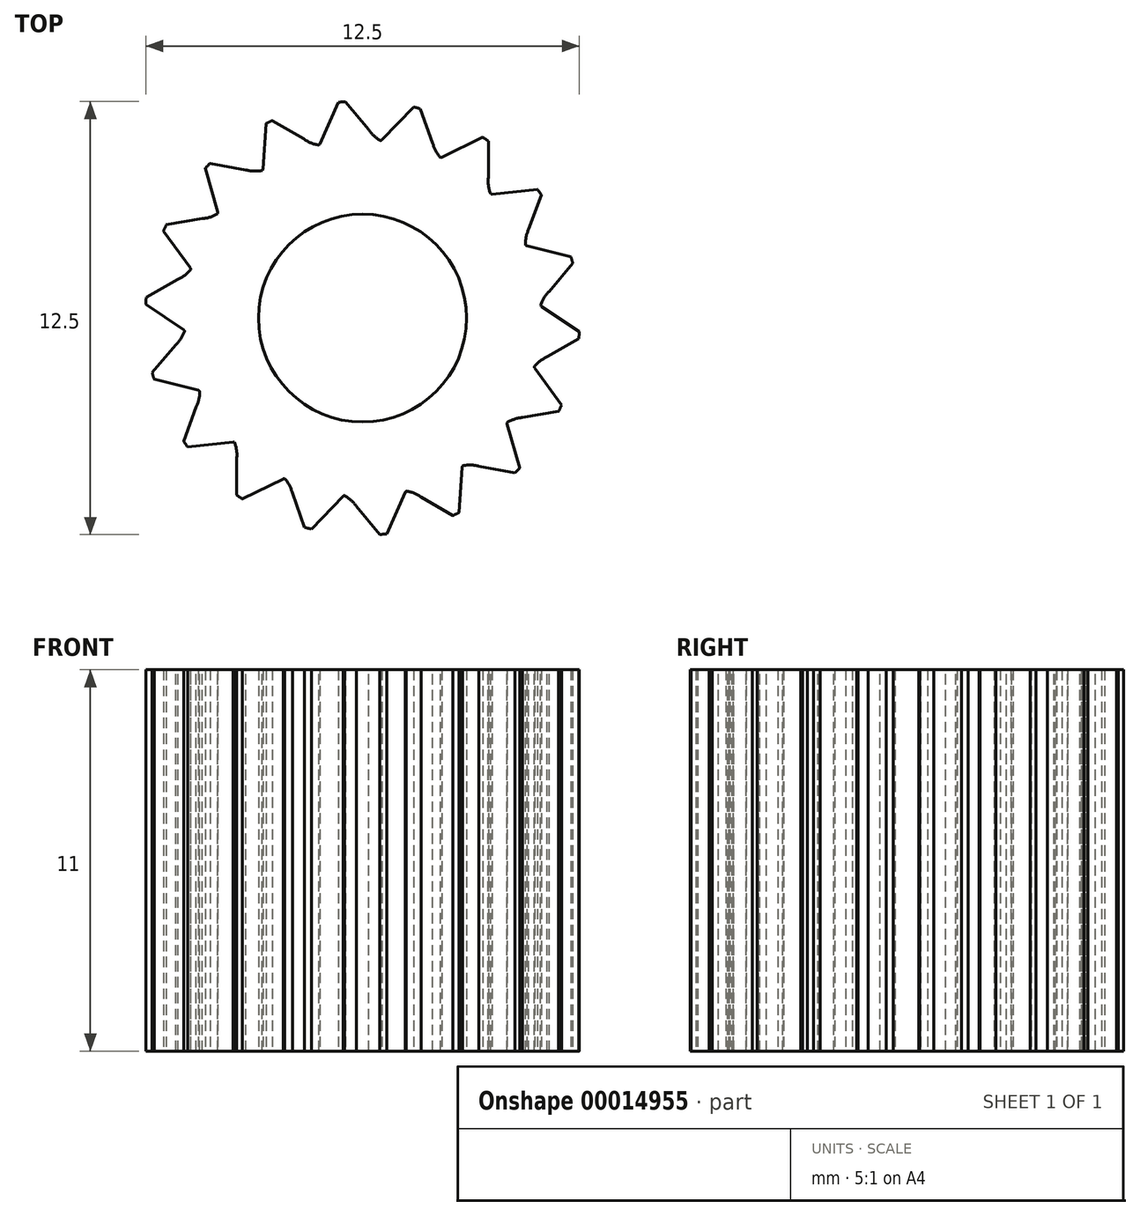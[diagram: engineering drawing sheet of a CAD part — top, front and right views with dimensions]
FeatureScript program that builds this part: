
annotation { "Feature Type Name" : "Feature", "Feature Type Description" : "" }
export const myFeature = defineFeature(function(context is Context, id is Id, definition is map)
    precondition{}
    {
        {
            var Q0;
            Q0=qCreatedBy(makeId("Top.planeOp"),FACE);
            var sketch = newSketch(context, id + "F0", { "sketchPlane" : qUnion([Q0])});
            skCircle(sketch, "E0", {"center": v(0, 0) * mm, "radius": 3 * mm});
            skCircle(sketch, "E1", {"center": v(0, 0) * mm, "radius": 6.26 * mm});
            skSolve(sketch);
        }
        {
            var Q0;
            Q0=qSketchRegion(id+"F0",true);
            extrude(context, id + "F1", {"entities" : qUnion([Q0]), "depth" : 11 * mm});
        }
        {
            var Q0;
            Q0=qCreatedBy(makeId("Front.planeOp"),FACE);
            cPlane(context, id + "F2", {"entities" : qUnion([Q0]), "cplaneType" : CPlaneType.OFFSET, "offset" : 5 * mm, "width" : 150 * mm, "height" : 150 * mm});
        }
        {
            var Q0;
            Q0=qCreatedBy(id+"F2.planeOp",FACE);
            var sketch = newSketch(context, id + "F3", { "sketchPlane" : qUnion([Q0])});
            skLineSegment(sketch, "E2.bottom", {"start": v(0, 11.05) * mm, "end": v(-1.05, 11.05) * mm});
            skLineSegment(sketch, "E2.top", {"start": v(0, 0) * mm, "end": v(-1.05, 0) * mm});
            skLineSegment(sketch, "E2.left", {"start": v(0, 11.05) * mm, "end": v(0, 0) * mm});
            skLineSegment(sketch, "E2.right", {"start": v(-1.05, 11.05) * mm, "end": v(-1.05, 0) * mm});
            skSolve(sketch);
        }
        {
            var Q0;
            Q0=makeQuery(id+"F3.imprint","IMPRINT",FACE,{"disambiguationData":[TD([[makeQuery(id+"F3.imprint","IMPRINT",EDGE,{"derivedFrom":sQuery(id+"F3.wireOp",EDGE,"E2.bottom")}),1.0]])]});
            extrude(context, id + "F4", {"entities" : qUnion([Q0]), "depth" : 2 * mm});
        }
        {
            var Q0;
            Q0=makeQuery(id+"F4.opExtrude","CAP_EDGE",EDGE,{"disambiguationData":[OSD([sQuery(id+"F3.wireOp",EDGE,"E2.left")])],"isStart":true});
            var Q1;
            Q1=makeQuery(id+"F4.opExtrude","CAP_EDGE",EDGE,{"disambiguationData":[OSD([sQuery(id+"F3.wireOp",EDGE,"E2.right")])],"isStart":true});
            fillet(context, id + "F5", {"entities" : qUnion([Q0, Q1]), "radius" : 1 * mm, "tangentPropagation" : true, "allowEdgeOverflow" : false});
        }
        {
            var Q0;
            Q0=makeQuery(id+"F4.opExtrude","SWEPT_BODY",BODY,{"disambiguationData":[OSD([sQuery(id+"F3.wireOp",EDGE,"E2.bottom"),sQuery(id+"F3.wireOp",EDGE,"E2.top"),sQuery(id+"F3.wireOp",EDGE,"E2.left"),sQuery(id+"F3.wireOp",EDGE,"E2.right")])]});
            var Q1;
            Q1=makeQuery(id+"F1.opExtrude","SWEPT_FACE",FACE,{"disambiguationData":[OSD([sQuery(id+"F0.wireOp",EDGE,"E1")])]});
            circularPattern(context, id + "F6", {"operationType" : NewBodyOperationType.REMOVE, "entities" : qUnion([Q0]), "axis" : qUnion([Q1]), "angle" : 20 * degree, "instanceCount" : round(20)});
        }
        {
            var Q0;
            Q0=makeQuery(id+"F6.boolean.opBoolean","INTERSECT",EDGE,{"derivedFrom":[makeQuery(id+"F1.opExtrude","SWEPT_FACE",FACE,{"disambiguationData":[OSD([sQuery(id+"F0.wireOp",EDGE,"E1")])]}),makeQuery(id+"F6.opPattern","COPY",FACE,{"derivedFrom":makeQuery(id+"F4.opExtrude","SWEPT_FACE",FACE,{"disambiguationData":[OSD([sQuery(id+"F3.wireOp",EDGE,"E2.left")])]}),"instanceName":"1"})]});
            var Q1;
            Q1=makeQuery(id+"F6.boolean.opBoolean","INTERSECT",EDGE,{"derivedFrom":[makeQuery(id+"F1.opExtrude","SWEPT_FACE",FACE,{"disambiguationData":[OSD([sQuery(id+"F0.wireOp",EDGE,"E1")])]}),makeQuery(id+"F4.opExtrude","SWEPT_FACE",FACE,{"disambiguationData":[OSD([sQuery(id+"F3.wireOp",EDGE,"E2.left")])]})]});
            var Q2;
            Q2=makeQuery(id+"F6.boolean.opBoolean","INTERSECT",EDGE,{"derivedFrom":[makeQuery(id+"F1.opExtrude","SWEPT_FACE",FACE,{"disambiguationData":[OSD([sQuery(id+"F0.wireOp",EDGE,"E1")])]}),makeQuery(id+"F6.opPattern","COPY",FACE,{"derivedFrom":makeQuery(id+"F4.opExtrude","SWEPT_FACE",FACE,{"disambiguationData":[OSD([sQuery(id+"F3.wireOp",EDGE,"E2.left")])]}),"instanceName":"17"})]});
            var Q3;
            Q3=makeQuery(id+"F6.boolean.opBoolean","INTERSECT",EDGE,{"derivedFrom":[makeQuery(id+"F1.opExtrude","SWEPT_FACE",FACE,{"disambiguationData":[OSD([sQuery(id+"F0.wireOp",EDGE,"E1")])]}),makeQuery(id+"F6.opPattern","COPY",FACE,{"derivedFrom":makeQuery(id+"F4.opExtrude","SWEPT_FACE",FACE,{"disambiguationData":[OSD([sQuery(id+"F3.wireOp",EDGE,"E2.left")])]}),"instanceName":"16"})]});
            var Q4;
            Q4=makeQuery(id+"F6.boolean.opBoolean","INTERSECT",EDGE,{"derivedFrom":[makeQuery(id+"F1.opExtrude","SWEPT_FACE",FACE,{"disambiguationData":[OSD([sQuery(id+"F0.wireOp",EDGE,"E1")])]}),makeQuery(id+"F6.opPattern","COPY",FACE,{"derivedFrom":makeQuery(id+"F4.opExtrude","SWEPT_FACE",FACE,{"disambiguationData":[OSD([sQuery(id+"F3.wireOp",EDGE,"E2.left")])]}),"instanceName":"2"})]});
            var Q5;
            Q5=makeQuery(id+"F6.boolean.opBoolean","INTERSECT",EDGE,{"derivedFrom":[makeQuery(id+"F1.opExtrude","SWEPT_FACE",FACE,{"disambiguationData":[OSD([sQuery(id+"F0.wireOp",EDGE,"E1")])]}),makeQuery(id+"F6.opPattern","COPY",FACE,{"derivedFrom":makeQuery(id+"F4.opExtrude","SWEPT_FACE",FACE,{"disambiguationData":[OSD([sQuery(id+"F3.wireOp",EDGE,"E2.left")])]}),"instanceName":"15"})]});
            var Q6;
            Q6=makeQuery(id+"F6.boolean.opBoolean","INTERSECT",EDGE,{"derivedFrom":[makeQuery(id+"F1.opExtrude","SWEPT_FACE",FACE,{"disambiguationData":[OSD([sQuery(id+"F0.wireOp",EDGE,"E1")])]}),makeQuery(id+"F6.opPattern","COPY",FACE,{"derivedFrom":makeQuery(id+"F4.opExtrude","SWEPT_FACE",FACE,{"disambiguationData":[OSD([sQuery(id+"F3.wireOp",EDGE,"E2.left")])]}),"instanceName":"14"})]});
            var Q7;
            Q7=makeQuery(id+"F6.boolean.opBoolean","INTERSECT",EDGE,{"derivedFrom":[makeQuery(id+"F1.opExtrude","SWEPT_FACE",FACE,{"disambiguationData":[OSD([sQuery(id+"F0.wireOp",EDGE,"E1")])]}),makeQuery(id+"F6.opPattern","COPY",FACE,{"derivedFrom":makeQuery(id+"F4.opExtrude","SWEPT_FACE",FACE,{"disambiguationData":[OSD([sQuery(id+"F3.wireOp",EDGE,"E2.left")])]}),"instanceName":"3"})]});
            var Q8;
            Q8=makeQuery(id+"F6.boolean.opBoolean","INTERSECT",EDGE,{"derivedFrom":[makeQuery(id+"F1.opExtrude","SWEPT_FACE",FACE,{"disambiguationData":[OSD([sQuery(id+"F0.wireOp",EDGE,"E1")])]}),makeQuery(id+"F6.opPattern","COPY",FACE,{"derivedFrom":makeQuery(id+"F4.opExtrude","SWEPT_FACE",FACE,{"disambiguationData":[OSD([sQuery(id+"F3.wireOp",EDGE,"E2.left")])]}),"instanceName":"4"})]});
            var Q9;
            Q9=makeQuery(id+"F6.boolean.opBoolean","INTERSECT",EDGE,{"derivedFrom":[makeQuery(id+"F1.opExtrude","SWEPT_FACE",FACE,{"disambiguationData":[OSD([sQuery(id+"F0.wireOp",EDGE,"E1")])]}),makeQuery(id+"F6.opPattern","COPY",FACE,{"derivedFrom":makeQuery(id+"F4.opExtrude","SWEPT_FACE",FACE,{"disambiguationData":[OSD([sQuery(id+"F3.wireOp",EDGE,"E2.left")])]}),"instanceName":"13"})]});
            var Q10;
            Q10=makeQuery(id+"F6.boolean.opBoolean","INTERSECT",EDGE,{"derivedFrom":[makeQuery(id+"F1.opExtrude","SWEPT_FACE",FACE,{"disambiguationData":[OSD([sQuery(id+"F0.wireOp",EDGE,"E1")])]}),makeQuery(id+"F6.opPattern","COPY",FACE,{"derivedFrom":makeQuery(id+"F4.opExtrude","SWEPT_FACE",FACE,{"disambiguationData":[OSD([sQuery(id+"F3.wireOp",EDGE,"E2.left")])]}),"instanceName":"12"})]});
            var Q11;
            Q11=makeQuery(id+"F6.boolean.opBoolean","INTERSECT",EDGE,{"derivedFrom":[makeQuery(id+"F1.opExtrude","SWEPT_FACE",FACE,{"disambiguationData":[OSD([sQuery(id+"F0.wireOp",EDGE,"E1")])]}),makeQuery(id+"F6.opPattern","COPY",FACE,{"derivedFrom":makeQuery(id+"F4.opExtrude","SWEPT_FACE",FACE,{"disambiguationData":[OSD([sQuery(id+"F3.wireOp",EDGE,"E2.left")])]}),"instanceName":"11"})]});
            var Q12;
            Q12=makeQuery(id+"F6.boolean.opBoolean","INTERSECT",EDGE,{"derivedFrom":[makeQuery(id+"F1.opExtrude","SWEPT_FACE",FACE,{"disambiguationData":[OSD([sQuery(id+"F0.wireOp",EDGE,"E1")])]}),makeQuery(id+"F6.opPattern","COPY",FACE,{"derivedFrom":makeQuery(id+"F4.opExtrude","SWEPT_FACE",FACE,{"disambiguationData":[OSD([sQuery(id+"F3.wireOp",EDGE,"E2.left")])]}),"instanceName":"10"})]});
            var Q13;
            Q13=makeQuery(id+"F6.boolean.opBoolean","INTERSECT",EDGE,{"derivedFrom":[makeQuery(id+"F1.opExtrude","SWEPT_FACE",FACE,{"disambiguationData":[OSD([sQuery(id+"F0.wireOp",EDGE,"E1")])]}),makeQuery(id+"F6.opPattern","COPY",FACE,{"derivedFrom":makeQuery(id+"F4.opExtrude","SWEPT_FACE",FACE,{"disambiguationData":[OSD([sQuery(id+"F3.wireOp",EDGE,"E2.left")])]}),"instanceName":"9"})]});
            var Q14;
            Q14=makeQuery(id+"F6.boolean.opBoolean","INTERSECT",EDGE,{"derivedFrom":[makeQuery(id+"F1.opExtrude","SWEPT_FACE",FACE,{"disambiguationData":[OSD([sQuery(id+"F0.wireOp",EDGE,"E1")])]}),makeQuery(id+"F6.opPattern","COPY",FACE,{"derivedFrom":makeQuery(id+"F4.opExtrude","SWEPT_FACE",FACE,{"disambiguationData":[OSD([sQuery(id+"F3.wireOp",EDGE,"E2.left")])]}),"instanceName":"8"})]});
            var Q15;
            Q15=makeQuery(id+"F6.boolean.opBoolean","INTERSECT",EDGE,{"derivedFrom":[makeQuery(id+"F1.opExtrude","SWEPT_FACE",FACE,{"disambiguationData":[OSD([sQuery(id+"F0.wireOp",EDGE,"E1")])]}),makeQuery(id+"F6.opPattern","COPY",FACE,{"derivedFrom":makeQuery(id+"F4.opExtrude","SWEPT_FACE",FACE,{"disambiguationData":[OSD([sQuery(id+"F3.wireOp",EDGE,"E2.left")])]}),"instanceName":"7"})]});
            var Q16;
            Q16=makeQuery(id+"F6.boolean.opBoolean","INTERSECT",EDGE,{"derivedFrom":[makeQuery(id+"F1.opExtrude","SWEPT_FACE",FACE,{"disambiguationData":[OSD([sQuery(id+"F0.wireOp",EDGE,"E1")])]}),makeQuery(id+"F6.opPattern","COPY",FACE,{"derivedFrom":makeQuery(id+"F4.opExtrude","SWEPT_FACE",FACE,{"disambiguationData":[OSD([sQuery(id+"F3.wireOp",EDGE,"E2.left")])]}),"instanceName":"6"})]});
            var Q17;
            Q17=makeQuery(id+"F6.boolean.opBoolean","INTERSECT",EDGE,{"derivedFrom":[makeQuery(id+"F1.opExtrude","SWEPT_FACE",FACE,{"disambiguationData":[OSD([sQuery(id+"F0.wireOp",EDGE,"E1")])]}),makeQuery(id+"F6.opPattern","COPY",FACE,{"derivedFrom":makeQuery(id+"F4.opExtrude","SWEPT_FACE",FACE,{"disambiguationData":[OSD([sQuery(id+"F3.wireOp",EDGE,"E2.left")])]}),"instanceName":"5"})]});
            chamfer(context, id + "F7", {"entities" : qUnion([Q0, Q1, Q2, Q3, Q4, Q5, Q6, Q7, Q8, Q9, Q10, Q11, Q12, Q13, Q14, Q15, Q16, Q17]), "chamferType" : ChamferType.OFFSET_ANGLE, "width" : 0.7 * mm, "oppositeDirection" : false, "angle" : 60 * degree, "tangentPropagation" : true});
        }
        {
            var Q0;
            Q0=makeQuery(id+"F6.boolean.opBoolean","INTERSECT",EDGE,{"derivedFrom":[makeQuery(id+"F1.opExtrude","SWEPT_FACE",FACE,{"disambiguationData":[OSD([sQuery(id+"F0.wireOp",EDGE,"E1")])]}),makeQuery(id+"F6.opPattern","COPY",FACE,{"derivedFrom":makeQuery(id+"F4.opExtrude","SWEPT_FACE",FACE,{"disambiguationData":[OSD([sQuery(id+"F3.wireOp",EDGE,"E2.right")])]}),"instanceName":"3"})]});
            var Q1;
            Q1=makeQuery(id+"F6.boolean.opBoolean","INTERSECT",EDGE,{"derivedFrom":[makeQuery(id+"F1.opExtrude","SWEPT_FACE",FACE,{"disambiguationData":[OSD([sQuery(id+"F0.wireOp",EDGE,"E1")])]}),makeQuery(id+"F6.opPattern","COPY",FACE,{"derivedFrom":makeQuery(id+"F4.opExtrude","SWEPT_FACE",FACE,{"disambiguationData":[OSD([sQuery(id+"F3.wireOp",EDGE,"E2.right")])]}),"instanceName":"4"})]});
            var Q2;
            Q2=makeQuery(id+"F6.boolean.opBoolean","INTERSECT",EDGE,{"derivedFrom":[makeQuery(id+"F1.opExtrude","SWEPT_FACE",FACE,{"disambiguationData":[OSD([sQuery(id+"F0.wireOp",EDGE,"E1")])]}),makeQuery(id+"F6.opPattern","COPY",FACE,{"derivedFrom":makeQuery(id+"F4.opExtrude","SWEPT_FACE",FACE,{"disambiguationData":[OSD([sQuery(id+"F3.wireOp",EDGE,"E2.right")])]}),"instanceName":"5"})]});
            var Q3;
            Q3=makeQuery(id+"F6.boolean.opBoolean","INTERSECT",EDGE,{"derivedFrom":[makeQuery(id+"F1.opExtrude","SWEPT_FACE",FACE,{"disambiguationData":[OSD([sQuery(id+"F0.wireOp",EDGE,"E1")])]}),makeQuery(id+"F6.opPattern","COPY",FACE,{"derivedFrom":makeQuery(id+"F4.opExtrude","SWEPT_FACE",FACE,{"disambiguationData":[OSD([sQuery(id+"F3.wireOp",EDGE,"E2.right")])]}),"instanceName":"6"})]});
            var Q4;
            Q4=makeQuery(id+"F6.boolean.opBoolean","INTERSECT",EDGE,{"derivedFrom":[makeQuery(id+"F1.opExtrude","SWEPT_FACE",FACE,{"disambiguationData":[OSD([sQuery(id+"F0.wireOp",EDGE,"E1")])]}),makeQuery(id+"F6.opPattern","COPY",FACE,{"derivedFrom":makeQuery(id+"F4.opExtrude","SWEPT_FACE",FACE,{"disambiguationData":[OSD([sQuery(id+"F3.wireOp",EDGE,"E2.right")])]}),"instanceName":"2"})]});
            var Q5;
            Q5=makeQuery(id+"F6.boolean.opBoolean","INTERSECT",EDGE,{"derivedFrom":[makeQuery(id+"F1.opExtrude","SWEPT_FACE",FACE,{"disambiguationData":[OSD([sQuery(id+"F0.wireOp",EDGE,"E1")])]}),makeQuery(id+"F6.opPattern","COPY",FACE,{"derivedFrom":makeQuery(id+"F4.opExtrude","SWEPT_FACE",FACE,{"disambiguationData":[OSD([sQuery(id+"F3.wireOp",EDGE,"E2.right")])]}),"instanceName":"1"})]});
            var Q6;
            Q6=makeQuery(id+"F6.boolean.opBoolean","INTERSECT",EDGE,{"derivedFrom":[makeQuery(id+"F1.opExtrude","SWEPT_FACE",FACE,{"disambiguationData":[OSD([sQuery(id+"F0.wireOp",EDGE,"E1")])]}),makeQuery(id+"F4.opExtrude","SWEPT_FACE",FACE,{"disambiguationData":[OSD([sQuery(id+"F3.wireOp",EDGE,"E2.right")])]})]});
            var Q7;
            Q7=makeQuery(id+"F6.boolean.opBoolean","INTERSECT",EDGE,{"derivedFrom":[makeQuery(id+"F1.opExtrude","SWEPT_FACE",FACE,{"disambiguationData":[OSD([sQuery(id+"F0.wireOp",EDGE,"E1")])]}),makeQuery(id+"F6.opPattern","COPY",FACE,{"derivedFrom":makeQuery(id+"F4.opExtrude","SWEPT_FACE",FACE,{"disambiguationData":[OSD([sQuery(id+"F3.wireOp",EDGE,"E2.right")])]}),"instanceName":"17"})]});
            var Q8;
            Q8=makeQuery(id+"F6.boolean.opBoolean","INTERSECT",EDGE,{"derivedFrom":[makeQuery(id+"F1.opExtrude","SWEPT_FACE",FACE,{"disambiguationData":[OSD([sQuery(id+"F0.wireOp",EDGE,"E1")])]}),makeQuery(id+"F6.opPattern","COPY",FACE,{"derivedFrom":makeQuery(id+"F4.opExtrude","SWEPT_FACE",FACE,{"disambiguationData":[OSD([sQuery(id+"F3.wireOp",EDGE,"E2.right")])]}),"instanceName":"16"})]});
            var Q9;
            Q9=makeQuery(id+"F6.boolean.opBoolean","INTERSECT",EDGE,{"derivedFrom":[makeQuery(id+"F1.opExtrude","SWEPT_FACE",FACE,{"disambiguationData":[OSD([sQuery(id+"F0.wireOp",EDGE,"E1")])]}),makeQuery(id+"F6.opPattern","COPY",FACE,{"derivedFrom":makeQuery(id+"F4.opExtrude","SWEPT_FACE",FACE,{"disambiguationData":[OSD([sQuery(id+"F3.wireOp",EDGE,"E2.right")])]}),"instanceName":"15"})]});
            var Q10;
            Q10=makeQuery(id+"F6.boolean.opBoolean","INTERSECT",EDGE,{"derivedFrom":[makeQuery(id+"F1.opExtrude","SWEPT_FACE",FACE,{"disambiguationData":[OSD([sQuery(id+"F0.wireOp",EDGE,"E1")])]}),makeQuery(id+"F6.opPattern","COPY",FACE,{"derivedFrom":makeQuery(id+"F4.opExtrude","SWEPT_FACE",FACE,{"disambiguationData":[OSD([sQuery(id+"F3.wireOp",EDGE,"E2.right")])]}),"instanceName":"14"})]});
            var Q11;
            Q11=makeQuery(id+"F6.boolean.opBoolean","INTERSECT",EDGE,{"derivedFrom":[makeQuery(id+"F1.opExtrude","SWEPT_FACE",FACE,{"disambiguationData":[OSD([sQuery(id+"F0.wireOp",EDGE,"E1")])]}),makeQuery(id+"F6.opPattern","COPY",FACE,{"derivedFrom":makeQuery(id+"F4.opExtrude","SWEPT_FACE",FACE,{"disambiguationData":[OSD([sQuery(id+"F3.wireOp",EDGE,"E2.right")])]}),"instanceName":"12"})]});
            var Q12;
            Q12=makeQuery(id+"F6.boolean.opBoolean","INTERSECT",EDGE,{"derivedFrom":[makeQuery(id+"F1.opExtrude","SWEPT_FACE",FACE,{"disambiguationData":[OSD([sQuery(id+"F0.wireOp",EDGE,"E1")])]}),makeQuery(id+"F6.opPattern","COPY",FACE,{"derivedFrom":makeQuery(id+"F4.opExtrude","SWEPT_FACE",FACE,{"disambiguationData":[OSD([sQuery(id+"F3.wireOp",EDGE,"E2.right")])]}),"instanceName":"11"})]});
            var Q13;
            Q13=makeQuery(id+"F6.boolean.opBoolean","INTERSECT",EDGE,{"derivedFrom":[makeQuery(id+"F1.opExtrude","SWEPT_FACE",FACE,{"disambiguationData":[OSD([sQuery(id+"F0.wireOp",EDGE,"E1")])]}),makeQuery(id+"F6.opPattern","COPY",FACE,{"derivedFrom":makeQuery(id+"F4.opExtrude","SWEPT_FACE",FACE,{"disambiguationData":[OSD([sQuery(id+"F3.wireOp",EDGE,"E2.right")])]}),"instanceName":"10"})]});
            var Q14;
            Q14=makeQuery(id+"F6.boolean.opBoolean","INTERSECT",EDGE,{"derivedFrom":[makeQuery(id+"F1.opExtrude","SWEPT_FACE",FACE,{"disambiguationData":[OSD([sQuery(id+"F0.wireOp",EDGE,"E1")])]}),makeQuery(id+"F6.opPattern","COPY",FACE,{"derivedFrom":makeQuery(id+"F4.opExtrude","SWEPT_FACE",FACE,{"disambiguationData":[OSD([sQuery(id+"F3.wireOp",EDGE,"E2.right")])]}),"instanceName":"9"})]});
            var Q15;
            Q15=makeQuery(id+"F6.boolean.opBoolean","INTERSECT",EDGE,{"derivedFrom":[makeQuery(id+"F1.opExtrude","SWEPT_FACE",FACE,{"disambiguationData":[OSD([sQuery(id+"F0.wireOp",EDGE,"E1")])]}),makeQuery(id+"F6.opPattern","COPY",FACE,{"derivedFrom":makeQuery(id+"F4.opExtrude","SWEPT_FACE",FACE,{"disambiguationData":[OSD([sQuery(id+"F3.wireOp",EDGE,"E2.right")])]}),"instanceName":"8"})]});
            var Q16;
            Q16=makeQuery(id+"F6.boolean.opBoolean","INTERSECT",EDGE,{"derivedFrom":[makeQuery(id+"F1.opExtrude","SWEPT_FACE",FACE,{"disambiguationData":[OSD([sQuery(id+"F0.wireOp",EDGE,"E1")])]}),makeQuery(id+"F6.opPattern","COPY",FACE,{"derivedFrom":makeQuery(id+"F4.opExtrude","SWEPT_FACE",FACE,{"disambiguationData":[OSD([sQuery(id+"F3.wireOp",EDGE,"E2.right")])]}),"instanceName":"7"})]});
            var Q17;
            Q17=makeQuery(id+"F6.boolean.opBoolean","INTERSECT",EDGE,{"derivedFrom":[makeQuery(id+"F1.opExtrude","SWEPT_FACE",FACE,{"disambiguationData":[OSD([sQuery(id+"F0.wireOp",EDGE,"E1")])]}),makeQuery(id+"F6.opPattern","COPY",FACE,{"derivedFrom":makeQuery(id+"F4.opExtrude","SWEPT_FACE",FACE,{"disambiguationData":[OSD([sQuery(id+"F3.wireOp",EDGE,"E2.right")])]}),"instanceName":"13"})]});
            chamfer(context, id + "F8", {"entities" : qUnion([Q0, Q1, Q2, Q3, Q4, Q5, Q6, Q7, Q8, Q9, Q10, Q11, Q12, Q13, Q14, Q15, Q16, Q17]), "chamferType" : ChamferType.OFFSET_ANGLE, "width" : 2 * mm, "oppositeDirection" : false, "angle" : 35 * degree, "tangentPropagation" : true});
        }
    });
